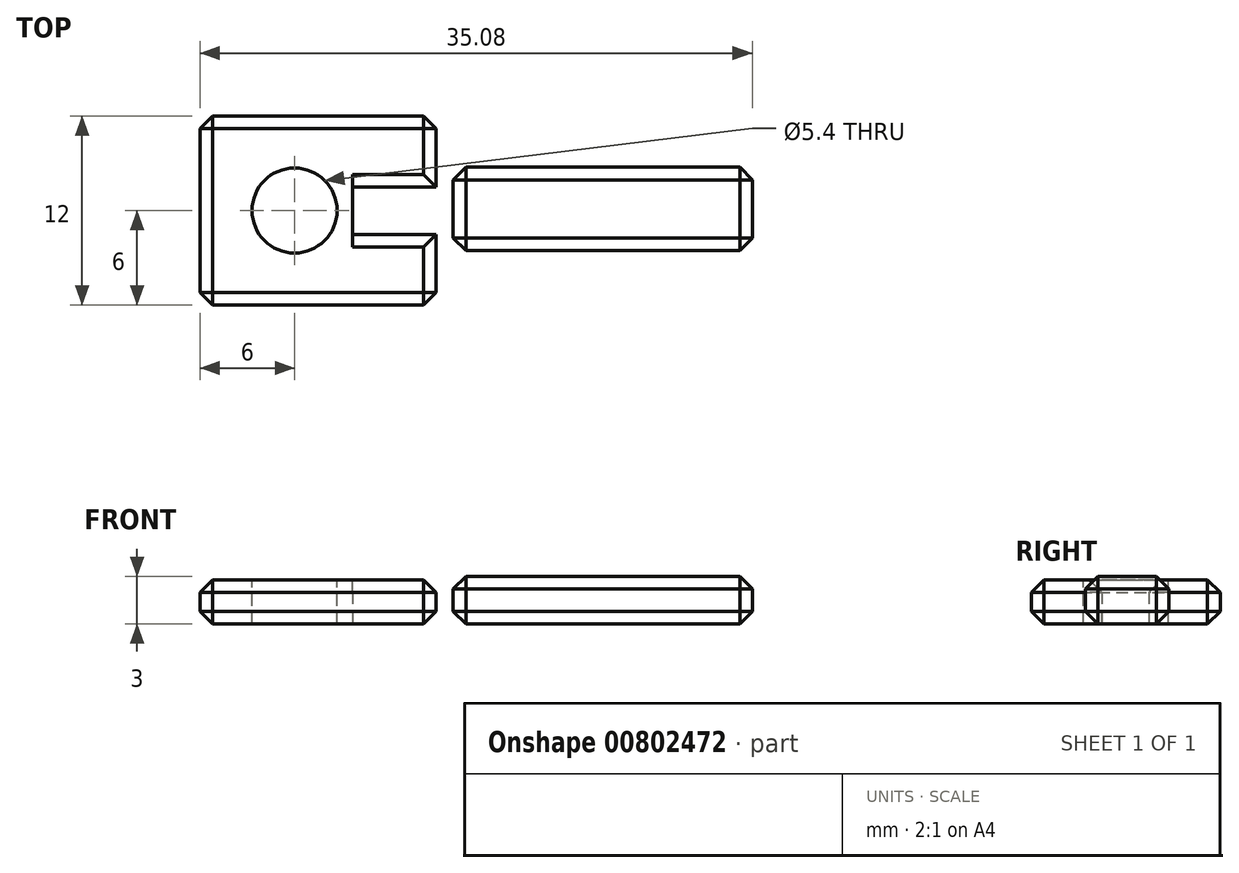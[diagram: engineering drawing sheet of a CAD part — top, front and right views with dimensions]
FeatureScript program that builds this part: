
annotation { "Feature Type Name" : "Feature", "Feature Type Description" : "" }
export const myFeature = defineFeature(function(context is Context, id is Id, definition is map)
    precondition{}
    {
        {
            var Q0;
            Q0=qCreatedBy(makeId("Top.planeOp"),FACE);
            var sketch = newSketch(context, id + "F0", { "sketchPlane" : qUnion([Q0])});
            skLineSegment(sketch, "E0.bottom", {"start": v(0, 0) * mm, "end": v(15, 0) * mm});
            skLineSegment(sketch, "E0.top", {"start": v(0, 12) * mm, "end": v(15, 12) * mm});
            skLineSegment(sketch, "E0.left", {"start": v(0, 0) * mm, "end": v(0, 12) * mm});
            skLineSegment(sketch, "E0.right", {"start": v(15, 0) * mm, "end": v(15, 12) * mm});
            skSolve(sketch);
        }
        {
            var Q0;
            Q0=makeQuery(id+"F0.imprint","IMPRINT",FACE,{"disambiguationData":[TD([[makeQuery(id+"F0.imprint","IMPRINT",EDGE,{"derivedFrom":sQuery(id+"F0.wireOp",EDGE,"E0.bottom")}),1.0]])]});
            extrude(context, id + "F1", {"entities" : qUnion([Q0]), "depth" : 2.8 * mm, "offsetDistance" : 25 * mm});
        }
        {
            var Q0;
            Q0=makeQuery(id+"F1.opExtrude","CAP_FACE",FACE,{"disambiguationData":[OSD([sQuery(id+"F0.wireOp",EDGE,"E0.bottom"),sQuery(id+"F0.wireOp",EDGE,"E0.top"),sQuery(id+"F0.wireOp",EDGE,"E0.left"),sQuery(id+"F0.wireOp",EDGE,"E0.right")])],"isStart":false});
            var sketch = newSketch(context, id + "F2", { "sketchPlane" : qUnion([Q0])});
            skCircle(sketch, "E1", {"center": v(6, 6) * mm, "radius": 2.7 * mm});
            skSolve(sketch);
        }
        {
            var Q0;
            Q0=makeQuery(id+"F2.imprint","IMPRINT",FACE,{"disambiguationData":[TD([[makeQuery(id+"F2.imprint","IMPRINT",EDGE,{"derivedFrom":sQuery(id+"F2.wireOp",EDGE,"E1")}),1.0]])]});
            extrude(context, id + "F3", {"entities" : qUnion([Q0]), "operationType" : NewBodyOperationType.REMOVE, "oppositeDirection" : true, "depth" : 25 * mm, "offsetDistance" : 25 * mm});
        }
        {
            var Q0;
            Q0=makeQuery(id+"F1.opExtrude","CAP_FACE",FACE,{"disambiguationData":[OSD([sQuery(id+"F0.wireOp",EDGE,"E0.bottom"),sQuery(id+"F0.wireOp",EDGE,"E0.top"),sQuery(id+"F0.wireOp",EDGE,"E0.left"),sQuery(id+"F0.wireOp",EDGE,"E0.right")])],"isStart":false});
            var sketch = newSketch(context, id + "F4", { "sketchPlane" : qUnion([Q0])});
            skLineSegment(sketch, "E2.bottom", {"start": v(9.7, 7.49) * mm, "end": v(15, 7.49) * mm});
            skLineSegment(sketch, "E2.top", {"start": v(9.7, 4.49) * mm, "end": v(15, 4.49) * mm});
            skLineSegment(sketch, "E2.left", {"start": v(9.7, 7.49) * mm, "end": v(9.7, 4.49) * mm});
            skLineSegment(sketch, "E2.right", {"start": v(15, 7.49) * mm, "end": v(15, 4.49) * mm});
            skSolve(sketch);
        }
        {
            var Q0;
            Q0=makeQuery(id+"F4.imprint","IMPRINT",FACE,{"disambiguationData":[TD([[makeQuery(id+"F4.imprint","IMPRINT",EDGE,{"derivedFrom":sQuery(id+"F4.wireOp",EDGE,"E2.bottom")}),-1.0]])]});
            extrude(context, id + "F5", {"entities" : qUnion([Q0]), "operationType" : NewBodyOperationType.REMOVE, "endBound" : BoundingType.SYMMETRIC, "depth" : 6 * mm, "offsetDistance" : 25 * mm});
        }
        {
            var Q0;
            Q0=makeQuery(id+"F1.opExtrude","SWEPT_EDGE",EDGE,{"disambiguationData":[OSD([sQuery(id+"F0.wireOp",EDGE,"E0.bottom"),sQuery(id+"F0.wireOp",EDGE,"E0.left")])]});
            var Q1;
            Q1=makeQuery(id+"F1.opExtrude","CAP_EDGE",EDGE,{"disambiguationData":[OSD([sQuery(id+"F0.wireOp",EDGE,"E0.bottom")])],"isStart":false});
            var Q2;
            Q2=makeQuery(id+"F1.opExtrude","CAP_EDGE",EDGE,{"disambiguationData":[OSD([sQuery(id+"F0.wireOp",EDGE,"E0.bottom")])],"isStart":true});
            var Q3;
            Q3=makeQuery(id+"F1.opExtrude","SWEPT_EDGE",EDGE,{"disambiguationData":[OSD([sQuery(id+"F0.wireOp",EDGE,"E0.bottom"),sQuery(id+"F0.wireOp",EDGE,"E0.right")])]});
            var Q4;
            Q4=makeQuery(id+"F1.opExtrude","CAP_EDGE",EDGE,{"disambiguationData":[OSD([sQuery(id+"F0.wireOp",EDGE,"E0.left")])],"isStart":false});
            var Q5;
            Q5=makeQuery(id+"F1.opExtrude","CAP_EDGE",EDGE,{"disambiguationData":[OSD([sQuery(id+"F0.wireOp",EDGE,"E0.left")])],"isStart":true});
            var Q6;
            Q6=makeQuery(id+"F1.opExtrude","SWEPT_EDGE",EDGE,{"disambiguationData":[OSD([sQuery(id+"F0.wireOp",EDGE,"E0.top"),sQuery(id+"F0.wireOp",EDGE,"E0.left")])]});
            var Q7;
            Q7=makeQuery(id+"F1.opExtrude","CAP_EDGE",EDGE,{"disambiguationData":[OSD([sQuery(id+"F0.wireOp",EDGE,"E0.top")])],"isStart":false});
            var Q8;
            Q8=makeQuery(id+"F1.opExtrude","CAP_EDGE",EDGE,{"disambiguationData":[OSD([sQuery(id+"F0.wireOp",EDGE,"E0.top")])],"isStart":true});
            var Q9;
            Q9=makeQuery(id+"F1.opExtrude","SWEPT_EDGE",EDGE,{"disambiguationData":[OSD([sQuery(id+"F0.wireOp",EDGE,"E0.top"),sQuery(id+"F0.wireOp",EDGE,"E0.right")])]});
            var Q10;
            Q10=makeQuery(id+"F1.opExtrude","CAP_EDGE",EDGE,{"disambiguationData":[OSD([sQuery(id+"F0.wireOp",EDGE,"E0.right")])],"isStart":true});
            var Q11;
            {var subQ0=sQuery(id+"F0.wireOp",EDGE,"E0.right");var subQ1=sQuery(id+"F0.wireOp",EDGE,"E0.bottom");Q11=makeQuery(id+"F5.boolean.opBoolean","SPLIT",EDGE,{"disambiguationData":[TD([makeQuery(id+"F1.opExtrude","SWEPT_FACE",FACE,{"disambiguationData":[OSD([subQ1])]})])],"derivedFrom":makeQuery(id+"F1.opExtrude","CAP_EDGE",EDGE,{"disambiguationData":[OSD([subQ0])],"isStart":false})});}
            var Q12;
            {var subQ0=sQuery(id+"F0.wireOp",EDGE,"E0.right");var subQ1=sQuery(id+"F0.wireOp",EDGE,"E0.top");Q12=makeQuery(id+"F5.boolean.opBoolean","SPLIT",EDGE,{"disambiguationData":[TD([makeQuery(id+"F1.opExtrude","SWEPT_FACE",FACE,{"disambiguationData":[OSD([subQ1])]})])],"derivedFrom":makeQuery(id+"F1.opExtrude","CAP_EDGE",EDGE,{"disambiguationData":[OSD([subQ0])],"isStart":false})});}
            var Q13;
            Q13=makeQuery(id+"F5.opExtrude","CAP_EDGE",EDGE,{"disambiguationData":[OSD([sQuery(id+"F4.wireOp",EDGE,"E2.top")])],"isStart":false});
            var Q14;
            Q14=makeQuery(id+"F5.opExtrude","SWEPT_EDGE",EDGE,{"disambiguationData":[OSD([sQuery(id+"F4.wireOp",EDGE,"E2.top"),sQuery(id+"F4.wireOp",EDGE,"E2.left")])]});
            var Q15;
            Q15=makeQuery(id+"F5.opExtrude","SWEPT_EDGE",EDGE,{"disambiguationData":[OSD([sQuery(id+"F4.wireOp",EDGE,"E2.bottom"),sQuery(id+"F4.wireOp",EDGE,"E2.left")])]});
            var Q16;
            Q16=makeQuery(id+"F5.opExtrude","CAP_EDGE",EDGE,{"disambiguationData":[OSD([sQuery(id+"F4.wireOp",EDGE,"E2.bottom")])],"isStart":false});
            var Q17;
            Q17=makeQuery(id+"F5.opExtrude","SWEPT_EDGE",EDGE,{"disambiguationData":[OSD([sQuery(id+"F0.wireOp",EDGE,"E0.right"),sQuery(id+"F4.wireOp",EDGE,"E2.bottom"),sQuery(id+"F4.wireOp",EDGE,"E2.right")])]});
            var Q18;
            Q18=makeQuery(id+"F5.opExtrude","SWEPT_EDGE",EDGE,{"disambiguationData":[OSD([sQuery(id+"F0.wireOp",EDGE,"E0.right"),sQuery(id+"F4.wireOp",EDGE,"E2.top"),sQuery(id+"F4.wireOp",EDGE,"E2.right")])]});
            var Q19;
            Q19=makeQuery(id+"F5.opExtrude","CAP_EDGE",EDGE,{"disambiguationData":[OSD([sQuery(id+"F4.wireOp",EDGE,"E2.right")])],"isStart":false});
            var Q20;
            Q20=makeQuery(id+"F3.boolean.opBoolean","COPY",EDGE,{"derivedFrom":makeQuery(id+"F3.opExtrude","CAP_EDGE",EDGE,{"disambiguationData":[OSD([sQuery(id+"F2.wireOp",EDGE,"E1")])],"isStart":true})});
            var Q21;
            Q21=makeQuery(id+"F5.opExtrude","CAP_EDGE",EDGE,{"disambiguationData":[OSD([sQuery(id+"F4.wireOp",EDGE,"E2.left")])],"isStart":false});
            var Q22;
            Q22=makeQuery(id+"F5.boolean.opBoolean","INTERSECT",EDGE,{"derivedFrom":[makeQuery(id+"F1.opExtrude","CAP_FACE",FACE,{"disambiguationData":[OSD([sQuery(id+"F0.wireOp",EDGE,"E0.bottom"),sQuery(id+"F0.wireOp",EDGE,"E0.top"),sQuery(id+"F0.wireOp",EDGE,"E0.left"),sQuery(id+"F0.wireOp",EDGE,"E0.right")])],"isStart":false}),makeQuery(id+"F5.opExtrude","SWEPT_FACE",FACE,{"disambiguationData":[OSD([sQuery(id+"F4.wireOp",EDGE,"E2.top")])]})]});
            var Q23;
            Q23=makeQuery(id+"F5.boolean.opBoolean","INTERSECT",EDGE,{"derivedFrom":[makeQuery(id+"F1.opExtrude","CAP_FACE",FACE,{"disambiguationData":[OSD([sQuery(id+"F0.wireOp",EDGE,"E0.bottom"),sQuery(id+"F0.wireOp",EDGE,"E0.top"),sQuery(id+"F0.wireOp",EDGE,"E0.left"),sQuery(id+"F0.wireOp",EDGE,"E0.right")])],"isStart":false}),makeQuery(id+"F5.opExtrude","SWEPT_FACE",FACE,{"disambiguationData":[OSD([sQuery(id+"F4.wireOp",EDGE,"E2.bottom")])]})]});
            chamfer(context, id + "F6", {"entities" : qUnion([Q0, Q1, Q2, Q3, Q4, Q5, Q6, Q7, Q8, Q9, Q10, Q11, Q12, Q13, Q14, Q15, Q16, Q17, Q18, Q19, Q20, Q21, Q22, Q23]), "width" : .8 * mm, "tangentPropagation" : true});
        }
        {
            var Q0;
            Q0=qCreatedBy(makeId("Top.planeOp"),FACE);
            var sketch = newSketch(context, id + "F7", { "sketchPlane" : qUnion([Q0])});
            skLineSegment(sketch, "E3.bottom", {"start": v(16.08, 8.75) * mm, "end": v(35.08, 8.75) * mm});
            skLineSegment(sketch, "E3.top", {"start": v(16.08, 3.45) * mm, "end": v(35.08, 3.45) * mm});
            skLineSegment(sketch, "E3.left", {"start": v(16.08, 8.75) * mm, "end": v(16.08, 3.45) * mm});
            skLineSegment(sketch, "E3.right", {"start": v(35.08, 8.75) * mm, "end": v(35.08, 3.45) * mm});
            skSolve(sketch);
        }
        {
            var Q0;
            Q0=makeQuery(id+"F7.imprint","IMPRINT",FACE,{"disambiguationData":[TD([[makeQuery(id+"F7.imprint","IMPRINT",EDGE,{"derivedFrom":sQuery(id+"F7.wireOp",EDGE,"E3.bottom")}),-1.0]])]});
            extrude(context, id + "F8", {"entities" : qUnion([Q0]), "depth" : 3 * mm, "offsetDistance" : 25 * mm});
        }
        {
            var Q0;
            Q0=makeQuery(id+"F8.opExtrude","CAP_EDGE",EDGE,{"disambiguationData":[OSD([sQuery(id+"F7.wireOp",EDGE,"E3.top")])],"isStart":false});
            var Q1;
            Q1=makeQuery(id+"F8.opExtrude","CAP_EDGE",EDGE,{"disambiguationData":[OSD([sQuery(id+"F7.wireOp",EDGE,"E3.right")])],"isStart":false});
            var Q2;
            Q2=makeQuery(id+"F8.opExtrude","CAP_EDGE",EDGE,{"disambiguationData":[OSD([sQuery(id+"F7.wireOp",EDGE,"E3.right")])],"isStart":true});
            var Q3;
            Q3=makeQuery(id+"F8.opExtrude","SWEPT_EDGE",EDGE,{"disambiguationData":[OSD([sQuery(id+"F7.wireOp",EDGE,"E3.top"),sQuery(id+"F7.wireOp",EDGE,"E3.right")])]});
            var Q4;
            Q4=makeQuery(id+"F8.opExtrude","SWEPT_EDGE",EDGE,{"disambiguationData":[OSD([sQuery(id+"F7.wireOp",EDGE,"E3.bottom"),sQuery(id+"F7.wireOp",EDGE,"E3.right")])]});
            var Q5;
            Q5=makeQuery(id+"F8.opExtrude","CAP_EDGE",EDGE,{"disambiguationData":[OSD([sQuery(id+"F7.wireOp",EDGE,"E3.top")])],"isStart":true});
            var Q6;
            Q6=makeQuery(id+"F8.opExtrude","SWEPT_EDGE",EDGE,{"disambiguationData":[OSD([sQuery(id+"F7.wireOp",EDGE,"E3.top"),sQuery(id+"F7.wireOp",EDGE,"E3.left")])]});
            var Q7;
            Q7=makeQuery(id+"F8.opExtrude","CAP_EDGE",EDGE,{"disambiguationData":[OSD([sQuery(id+"F7.wireOp",EDGE,"E3.bottom")])],"isStart":false});
            var Q8;
            Q8=makeQuery(id+"F8.opExtrude","CAP_EDGE",EDGE,{"disambiguationData":[OSD([sQuery(id+"F7.wireOp",EDGE,"E3.left")])],"isStart":true});
            var Q9;
            Q9=makeQuery(id+"F8.opExtrude","SWEPT_EDGE",EDGE,{"disambiguationData":[OSD([sQuery(id+"F7.wireOp",EDGE,"E3.bottom"),sQuery(id+"F7.wireOp",EDGE,"E3.left")])]});
            var Q10;
            Q10=makeQuery(id+"F8.opExtrude","CAP_EDGE",EDGE,{"disambiguationData":[OSD([sQuery(id+"F7.wireOp",EDGE,"E3.left")])],"isStart":false});
            var Q11;
            Q11=makeQuery(id+"F8.opExtrude","CAP_EDGE",EDGE,{"disambiguationData":[OSD([sQuery(id+"F7.wireOp",EDGE,"E3.bottom")])],"isStart":true});
            chamfer(context, id + "F9", {"entities" : qUnion([Q0, Q1, Q2, Q3, Q4, Q5, Q6, Q7, Q8, Q9, Q10, Q11]), "width" : .8 * mm, "tangentPropagation" : true});
        }
    });
